# Revit family: FP_Revit_18_CG905DNGX1_GasCooktop_9000xxxxA
name_source: partatom
category: Specialty Equipment
revit_build: Autodesk Revit 2018 (Build: 20170223_1515(x64)
units: mm (PartAtom-declared; Revit-internal decimal feet)

## family parameters
Always vertical = Yes
Cut with Voids When Loaded = Yes
OmniClass Number = 23.40.40.00
OmniClass Title = Food Service Equipment and Furnishings
Part Type = Normal
Room Calculation Point = No
Round Connector Dimension = Use Diameter
Shared = No
Work Plane-Based = No

## types (1)
- CG905DNGX1
    Cavity - Depth = 490 mm  [stored 1.60761 ft]
    Cavity - Height = 59 mm
    Cavity - Width = 865 mm  [stored 2.83793 ft]
    Chassis - Depth = 486 mm  [stored 1.59449 ft]
    Chassis - Height = 59 mm
    Chassis - Width = 856 mm  [stored 2.8084 ft]
    Clearance - Below Combustible = 81 mm  [stored 0.265748 ft]
    Clearance - Below Non-Combustible = 81 mm  [stored 0.265748 ft]
    Clearance - Overhead Combustible = 650 mm  [stored 2.13255 ft]
    Clearance - Overhead Non-Combustible = 500 mm  [stored 1.64042 ft]
    Clearance - Overhead Rangehood = 650 mm  [stored 2.13255 ft]
    Clearance - Rear Combustible = 115 mm  [stored 0.377297 ft]
    Clearance - Rear Non-Combustible = 35 mm  [stored 0.114829 ft]
    Clearance - Side Combustible = 100 mm  [stored 0.328084 ft]
    Connector Note - Electrical = 220-240 V, 50Hz, 10 A supply
    Connector Note - Gas = NG 20 mbar when operating at full, (50 mbar MAX), Connection is Rp 1/2" (ISO7-1)
    Description = 90cm Gas on Steel Hob
    Manufacturer = Fisher & Paykel Appliances
    Material - Body = Fisher & Paykel - Grey
    Material - Burners & Trivets = Fisher & Paykel - Black, Matte
    Material - Cooktop = Fisher & Paykel - Stainless Steel
    Material - Trim = Fisher & Paykel - Steel, Chrome Plated
    Model = CG905DNGX1
    Product - Depth = 530 mm  [stored 1.73885 ft]
    Product - Height = 109 mm
    Product - Width = 900 mm  [stored 2.95276 ft]
    URL = www.fisherpaykel.com
    Visibility - Clearance Required = Yes

note: [stored X ft] marks values corroborated as IEEE doubles in the binary element streams (Revit-internal decimal feet)

## geometry (parser evidence)
native form markers: Blend x20, Sweep x20
no freeform markers — native parametric forms only
